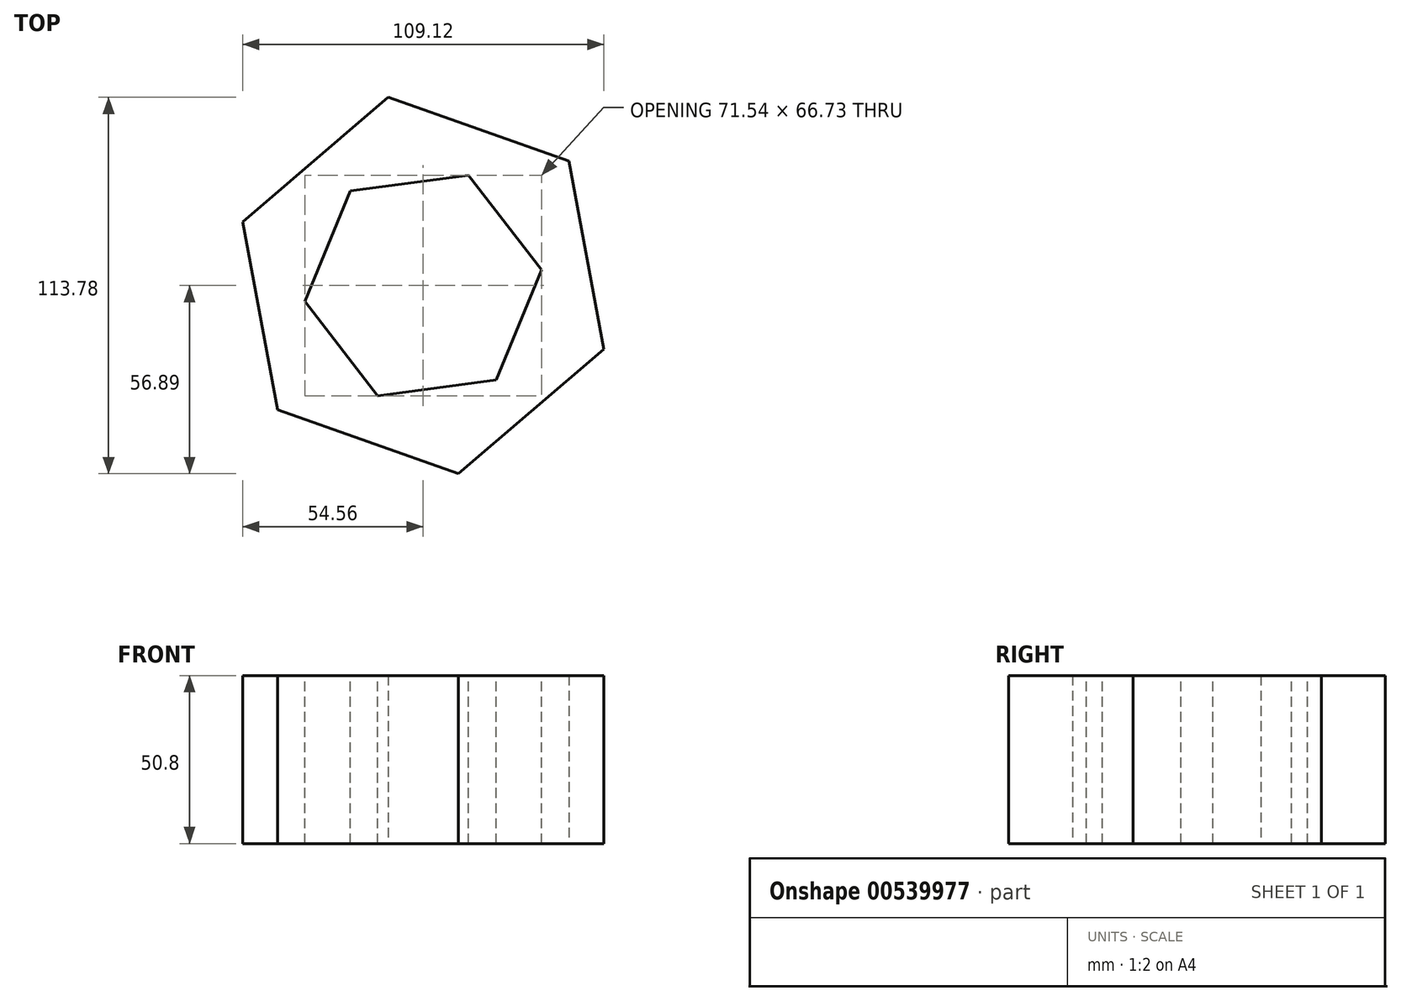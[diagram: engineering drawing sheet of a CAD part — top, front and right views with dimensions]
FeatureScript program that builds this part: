
annotation { "Feature Type Name" : "Feature", "Feature Type Description" : "" }
export const myFeature = defineFeature(function(context is Context, id is Id, definition is map)
    precondition{}
    {
        {
            var Q0;
            Q0=qCreatedBy(makeId("Top.planeOp"),FACE);
            var sketch = newSketch(context, id + "F0", { "sketchPlane" : qUnion([Q0])});
            skCircle(sketch, "E0.cCircle", {"center": v(0, 0) * mm, "radius": 50.11 * mm, "construction": true});
            skLineSegment(sketch, "E0.0", {"start": v(54.56, -19.28) * mm, "end": v(10.58, -56.89) * mm});
            skLineSegment(sketch, "E0.1", {"start": v(10.58, -56.89) * mm, "end": v(-43.97, -37.6) * mm});
            skLineSegment(sketch, "E0.2", {"start": v(-43.97, -37.6) * mm, "end": v(-54.56, 19.28) * mm});
            skLineSegment(sketch, "E0.3", {"start": v(-54.56, 19.28) * mm, "end": v(-10.58, 56.89) * mm});
            skLineSegment(sketch, "E0.4", {"start": v(-10.58, 56.89) * mm, "end": v(43.97, 37.6) * mm});
            skLineSegment(sketch, "E0.5", {"start": v(43.97, 37.6) * mm, "end": v(54.56, -19.28) * mm});
            skPoint(sketch, "E0.0.midPoint", {"position": v(32.57, -38.08) * mm});
            skSolve(sketch);
        }
        {
            var Q0;
            Q0=makeQuery(id+"F0.imprint","IMPRINT",FACE,{"disambiguationData":[TD([[makeQuery(id+"F0.imprint","IMPRINT",EDGE,{"derivedFrom":sQuery(id+"F0.wireOp",EDGE,"PQ4dUUgr-JXuE-Lszj-0ZTJ-GEu0R9Ruy4DC")}),1.0]])]});
            var Q1;
            Q1=makeQuery(id+"F0.imprint","IMPRINT",FACE,{"disambiguationData":[TD([[makeQuery(id+"F0.imprint","IMPRINT",EDGE,{"derivedFrom":sQuery(id+"F0.wireOp",EDGE,"E0.0")}),-1.0]])]});
            extrude(context, id + "F1", {"entities" : qUnion([Q0, Q1]), "depth" : 50.8 * mm, "offsetDistance" : 25.4 * mm});
        }
        {
            var Q0;
            Q0=makeQuery(id+"F1.opExtrude","CAP_FACE",FACE,{"disambiguationData":[OSD([sQuery(id+"F0.wireOp",EDGE,"E0.0"),sQuery(id+"F0.wireOp",EDGE,"E0.1"),sQuery(id+"F0.wireOp",EDGE,"E0.2"),sQuery(id+"F0.wireOp",EDGE,"E0.3"),sQuery(id+"F0.wireOp",EDGE,"E0.4"),sQuery(id+"F0.wireOp",EDGE,"E0.5")])],"isStart":false});
            var sketch = newSketch(context, id + "F2", { "sketchPlane" : qUnion([Q0])});
            skCircle(sketch, "E1.cCircle", {"center": v(0, 0) * mm, "radius": 31.25 * mm, "construction": true});
            skLineSegment(sketch, "E1.0", {"start": v(35.77, 4.78) * mm, "end": v(22.03, -28.58) * mm});
            skLineSegment(sketch, "E1.1", {"start": v(22.03, -28.58) * mm, "end": v(-13.74, -33.37) * mm});
            skLineSegment(sketch, "E1.2", {"start": v(-13.74, -33.37) * mm, "end": v(-35.77, -4.78) * mm});
            skLineSegment(sketch, "E1.3", {"start": v(-35.77, -4.78) * mm, "end": v(-22.03, 28.58) * mm});
            skLineSegment(sketch, "E1.4", {"start": v(-22.03, 28.58) * mm, "end": v(13.74, 33.37) * mm});
            skLineSegment(sketch, "E1.5", {"start": v(13.74, 33.37) * mm, "end": v(35.77, 4.78) * mm});
            skPoint(sketch, "E1.0.midPoint", {"position": v(28.9, -11.9) * mm});
            skSolve(sketch);
        }
        {
            var Q0;
            Q0 = qSketchRegion(id + "F2", true);
            extrude(context, id + "F3", {"entities" : qUnion([Q0]), "operationType" : NewBodyOperationType.REMOVE, "oppositeDirection" : true, "depth" : 50.8 * mm, "offsetDistance" : 25.4 * mm});
        }
    });
